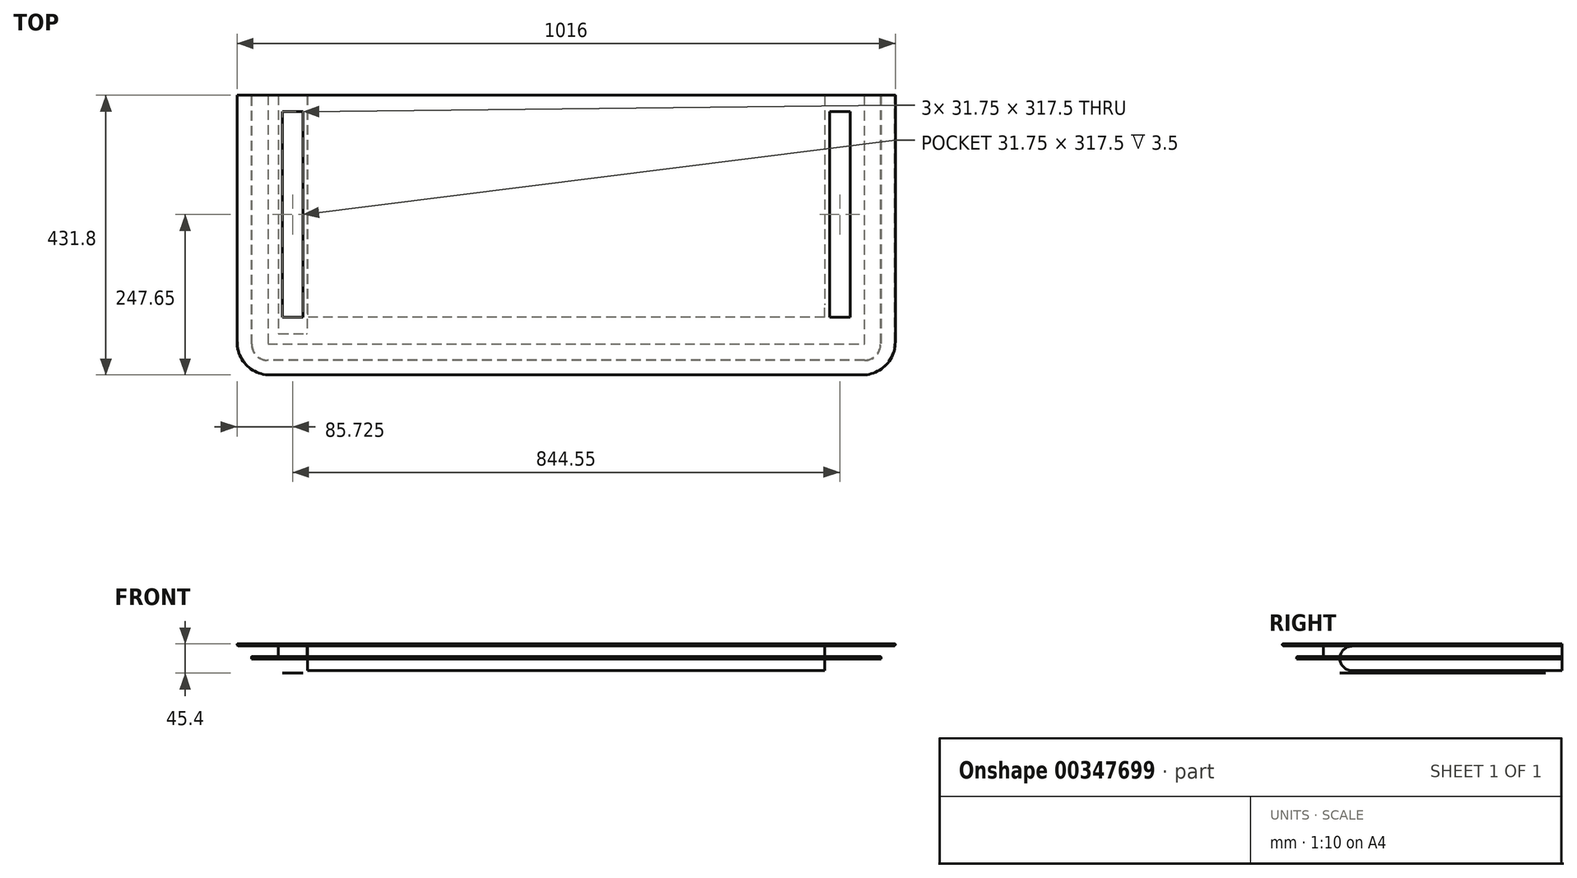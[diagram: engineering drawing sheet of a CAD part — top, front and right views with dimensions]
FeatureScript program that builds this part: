
annotation { "Feature Type Name" : "Feature", "Feature Type Description" : "" }
export const myFeature = defineFeature(function(context is Context, id is Id, definition is map)
    precondition{}
    {
        {
            assignVariable(context, id + "F0", {"name" : "TopThickness", "anyValue" : 2.5});
        }
        {
            assignVariable(context, id + "F1", {"name" : "LegWidth", "anyValue" : 1.75});
        }
        {
            assignVariable(context, id + "F2", {"name" : "CoveHeight", "anyValue" : 1});
        }
        {
            assignVariable(context, id + "F3", {"name" : "BottomThickness", "anyValue" : 1.5});
        }
        {
            assignVariable(context, id + "F4", {"name" : "BottomSkirtHeight", "anyValue" : 2});
        }
        {
            assignVariable(context, id + "F5", {"name" : "LegHeight", "anyValue" : 24 - getVariable(context, 'TopThickness') - 1.5 * getVariable(context, 'CoveHeight') - getVariable(context, 'BottomThickness') - getVariable(context, 'BottomSkirtHeight')});
        }
        {
            var Q0;
            Q0=qCreatedBy(makeId("Top.planeOp"),FACE);
            var sketch = newSketch(context, id + "F6", { "sketchPlane" : qUnion([Q0])});
            skLineSegment(sketch, "E0.bottom", {"start": v(0, 0) * mm, "end": v(1016, 0) * mm});
            skLineSegment(sketch, "E0.top", {"start": v(0, 431.8) * mm, "end": v(1016, 431.8) * mm});
            skLineSegment(sketch, "E0.left", {"start": v(0, 0) * mm, "end": v(0, 431.8) * mm});
            skLineSegment(sketch, "E0.right", {"start": v(1016, 0) * mm, "end": v(1016, 431.8) * mm});
            skSolve(sketch);
        }
        {
            var Q0;
            Q0 = qSketchRegion(id + "F6", true);
            extrude(context, id + "F7", {"entities" : qUnion([Q0]), "oppositeDirection" : true, "depth" : (getVariable(context, 'TopThickness')) * mm});
        }
        {
            var Q0;
            Q0=makeQuery(id+"F7.opExtrude","SWEPT_EDGE",EDGE,{"disambiguationData":[OSD([sQuery(id+"F6.wireOp",EDGE,"E0.bottom"),sQuery(id+"F6.wireOp",EDGE,"E0.left")])]});
            var Q1;
            Q1=makeQuery(id+"F7.opExtrude","SWEPT_EDGE",EDGE,{"disambiguationData":[OSD([sQuery(id+"F6.wireOp",EDGE,"E0.bottom"),sQuery(id+"F6.wireOp",EDGE,"E0.right")])]});
            fillet(context, id + "F8", {"entities" : qUnion([Q0, Q1]), "radius" : 50.8 * mm, "tangentPropagation" : true, "allowEdgeOverflow" : false});
        }
        {
            var Q0;
            Q0=makeQuery(id+"F7.opExtrude","CAP_EDGE",EDGE,{"disambiguationData":[OSD([sQuery(id+"F6.wireOp",EDGE,"E0.left")])],"isStart":true});
            var Q1;
            Q1=makeQuery(id+"F7.opExtrude","CAP_EDGE",EDGE,{"disambiguationData":[OSD([sQuery(id+"F6.wireOp",EDGE,"E0.left")])],"isStart":false});
            fillet(context, id + "F9", {"entities" : qUnion([Q0, Q1]), "radius" : (getVariable(context, 'TopThickness') / 2) * mm, "tangentPropagation" : true, "allowEdgeOverflow" : false});
        }
        {
            var Q0;
            Q0=makeQuery(id+"F7.opExtrude","CAP_FACE",FACE,{"disambiguationData":[OSD([sQuery(id+"F6.wireOp",EDGE,"E0.bottom"),sQuery(id+"F6.wireOp",EDGE,"E0.top"),sQuery(id+"F6.wireOp",EDGE,"E0.left"),sQuery(id+"F6.wireOp",EDGE,"E0.right")])],"isStart":false});
            extrude(context, id + "F10", {"entities" : qUnion([Q0]), "operationType" : NewBodyOperationType.ADD, "depth" : (getVariable(context, 'CoveHeight')) * mm});
        }
        {
            var Q0;
            Q0=makeQuery(id+"F10.opExtrude","CAP_FACE",FACE,{"disambiguationData":[OSD([sQuery(id+"F6.wireOp",EDGE,"E0.bottom"),sQuery(id+"F6.wireOp",EDGE,"E0.top"),sQuery(id+"F6.wireOp",EDGE,"E0.left"),sQuery(id+"F6.wireOp",EDGE,"E0.right")])],"isStart":false});
            var sketch = newSketch(context, id + "F11", { "sketchPlane" : qUnion([Q0])});
            skLineSegment(sketch, "E1.0", {"start": v(31.75, -50.8) * mm, "end": v(31.75, -431.8) * mm});
            skArc(sketch, "E1.1", {"start": v(50.8, -31.75) * mm, "mid": v(37.33, -37.33) * mm, "end": v(31.75, -50.8) * mm});
            skLineSegment(sketch, "E1.2", {"start": v(965.2, -31.75) * mm, "end": v(50.8, -31.75) * mm});
            skArc(sketch, "E1.3", {"start": v(984.25, -50.8) * mm, "mid": v(978.67, -37.33) * mm, "end": v(965.2, -31.75) * mm});
            skLineSegment(sketch, "E1.4", {"start": v(984.25, -431.8) * mm, "end": v(984.25, -50.8) * mm});
            skSolve(sketch);
        }
        {
            var Q0;
            {var subQ0=sQuery(id+"F6.wireOp",EDGE,"E0.top");Q0=makeQuery(id+"F10.boolean.opBoolean","MERGE",FACE,{"derivedFrom":[makeQuery(id+"F7.opExtrude","SWEPT_FACE",FACE,{"disambiguationData":[OSD([subQ0])]}),makeQuery(id+"F10.opExtrude","SWEPT_FACE",FACE,{"disambiguationData":[OSD([subQ0])]})]});}
            var sketch = newSketch(context, id + "F12", { "sketchPlane" : qUnion([Q0])});
            skCircle(sketch, "E2", {"center": v(-31.75, -88.9) * mm, "radius": 19.05 * mm});
            skSolve(sketch);
        }
        {
            var Q0;
            {var subQ0=sQuery(id+"F12.wireOp",EDGE,"E2");var subQ3=sQuery(id+"F6.wireOp",EDGE,"E0.top");var subQ7=makeQuery(id+"F10.opExtrude","CAP_EDGE",EDGE,{"disambiguationData":[OSD([subQ3])],"isStart":false});var subQ8=makeQuery(id+"F12.imprint","INTERSECT",VERTEX,{"derivedFrom":[subQ7,subQ0]});Q0=makeQuery(id+"F12.imprint","IMPRINT",FACE,{"disambiguationData":[TD([[makeQuery(id+"F12.imprint","IMPRINT",EDGE,{"disambiguationData":[TD([[subQ8,1.0]])],"derivedFrom":subQ0}),1.0]])]});}
            var Q1;
            Q1=sQuery(id+"F11.wireOp",EDGE,"E1.0");
            var Q2;
            Q2=sQuery(id+"F11.wireOp",EDGE,"E1.1");
            var Q3;
            Q3=sQuery(id+"F11.wireOp",EDGE,"E1.2");
            var Q4;
            Q4=sQuery(id+"F11.wireOp",EDGE,"E1.3");
            var Q5;
            Q5=sQuery(id+"F11.wireOp",EDGE,"E1.4");
            sweep(context, id + "F13", {"operationType" : NewBodyOperationType.REMOVE, "profiles" : qUnion([Q0]), "path" : qUnion([Q1, Q2, Q3, Q4, Q5])});
        }
        {
            var Q0;
            Q0=makeQuery(id+"F10.opExtrude","CAP_FACE",FACE,{"disambiguationData":[OSD([sQuery(id+"F6.wireOp",EDGE,"E0.bottom"),sQuery(id+"F6.wireOp",EDGE,"E0.top"),sQuery(id+"F6.wireOp",EDGE,"E0.left"),sQuery(id+"F6.wireOp",EDGE,"E0.right")])],"isStart":false});
            var sketch = newSketch(context, id + "F14", { "sketchPlane" : qUnion([Q0])});
            skLineSegment(sketch, "E3.bottom", {"start": v(63.5, -431.8) * mm, "end": v(107.95, -431.8) * mm});
            skLineSegment(sketch, "E3.top", {"start": v(63.5, -63.5) * mm, "end": v(107.95, -63.5) * mm});
            skLineSegment(sketch, "E3.left", {"start": v(63.5, -431.8) * mm, "end": v(63.5, -63.5) * mm});
            skLineSegment(sketch, "E3.right", {"start": v(107.95, -431.8) * mm, "end": v(107.95, -63.5) * mm});
            skSolve(sketch);
        }
        {
            var Q0;
            Q0 = qSketchRegion(id + "F14", true);
            extrude(context, id + "F15", {"entities" : qUnion([Q0]), "depth" : (getVariable(context, 'LegHeight')) * mm});
        }
        {
            var Q0;
            Q0=makeQuery(id+"F15.opExtrude","CAP_FACE",FACE,{"disambiguationData":[OSD([sQuery(id+"F14.wireOp",EDGE,"E3.bottom"),sQuery(id+"F14.wireOp",EDGE,"E3.top"),sQuery(id+"F14.wireOp",EDGE,"E3.left"),sQuery(id+"F14.wireOp",EDGE,"E3.right")])],"isStart":true});
            var sketch = newSketch(context, id + "F16", { "sketchPlane" : qUnion([Q0])});
            skLineSegment(sketch, "E4.bottom", {"start": v(69.85, 406.4) * mm, "end": v(101.6, 406.4) * mm});
            skLineSegment(sketch, "E4.top", {"start": v(69.85, 88.9) * mm, "end": v(101.6, 88.9) * mm});
            skLineSegment(sketch, "E4.left", {"start": v(69.85, 406.4) * mm, "end": v(69.85, 88.9) * mm});
            skLineSegment(sketch, "E4.right", {"start": v(101.6, 406.4) * mm, "end": v(101.6, 88.9) * mm});
            skSolve(sketch);
        }
        {
            var Q0;
            Q0 = qSketchRegion(id + "F16", true);
            extrude(context, id + "F17", {"entities" : qUnion([Q0]), "operationType" : NewBodyOperationType.ADD, "depth" : 25.4 * mm});
        }
        {
            var Q0;
            Q0=makeQuery(id+"F10.opExtrude","CAP_FACE",FACE,{"disambiguationData":[OSD([sQuery(id+"F6.wireOp",EDGE,"E0.bottom"),sQuery(id+"F6.wireOp",EDGE,"E0.top"),sQuery(id+"F6.wireOp",EDGE,"E0.left"),sQuery(id+"F6.wireOp",EDGE,"E0.right")])],"isStart":false});
            var sketch = newSketch(context, id + "F18", { "sketchPlane" : qUnion([Q0])});
            skLineSegment(sketch, "E5.0.0", {"start": v(69.85, -406.4) * mm, "end": v(69.85, -88.9) * mm});
            skLineSegment(sketch, "E5.0.1", {"start": v(69.85, -88.9) * mm, "end": v(101.6, -88.9) * mm});
            skLineSegment(sketch, "E5.0.2", {"start": v(101.6, -88.9) * mm, "end": v(101.6, -406.4) * mm});
            skLineSegment(sketch, "E5.0.3", {"start": v(101.6, -406.4) * mm, "end": v(69.85, -406.4) * mm});
            skLineSegment(sketch, "E6", {"start": v(508, -431.8) * mm, "end": v(508, 183.64) * mm, "construction": true});
            skLineSegment(sketch, "E7.MirrorCS", {"start": v(914.4, -406.4) * mm, "end": v(946.15, -406.4) * mm});
            skLineSegment(sketch, "E8.MirrorCS", {"start": v(946.15, -88.9) * mm, "end": v(914.4, -88.9) * mm});
            skLineSegment(sketch, "E9.MirrorCS", {"start": v(946.15, -406.4) * mm, "end": v(946.15, -88.9) * mm});
            skLineSegment(sketch, "E10.MirrorCS", {"start": v(914.4, -88.9) * mm, "end": v(914.4, -406.4) * mm});
            skSolve(sketch);
        }
        {
            var Q0;
            Q0 = qSketchRegion(id + "F18", true);
            extrude(context, id + "F19", {"entities" : qUnion([Q0]), "operationType" : NewBodyOperationType.REMOVE, "oppositeDirection" : true, "depth" : 25.4 * mm});
        }
        {
            var Q0;
            Q0=makeQuery(id+"F15.opExtrude","CAP_FACE",FACE,{"disambiguationData":[OSD([sQuery(id+"F14.wireOp",EDGE,"E3.bottom"),sQuery(id+"F14.wireOp",EDGE,"E3.top"),sQuery(id+"F14.wireOp",EDGE,"E3.left"),sQuery(id+"F14.wireOp",EDGE,"E3.right")])],"isStart":false});
            var sketch = newSketch(context, id + "F20", { "sketchPlane" : qUnion([Q0])});
            skLineSegment(sketch, "E11.0.0", {"start": v(69.85, -406.4) * mm, "end": v(69.85, -88.9) * mm});
            skLineSegment(sketch, "E11.0.1", {"start": v(69.85, -88.9) * mm, "end": v(101.6, -88.9) * mm});
            skLineSegment(sketch, "E11.0.2", {"start": v(101.6, -88.9) * mm, "end": v(101.6, -406.4) * mm});
            skLineSegment(sketch, "E11.0.3", {"start": v(101.6, -406.4) * mm, "end": v(69.85, -406.4) * mm});
            skSolve(sketch);
        }
        {
            var Q0;
            Q0 = qSketchRegion(id + "F20", true);
            extrude(context, id + "F21", {"entities" : qUnion([Q0]), "operationType" : NewBodyOperationType.ADD, "depth" : 25.4 * mm});
        }
        {
            var Q0;
            Q0=makeQuery(id+"F15.opExtrude","SWEPT_EDGE",EDGE,{"disambiguationData":[OSD([sQuery(id+"F14.wireOp",EDGE,"E3.top"),sQuery(id+"F14.wireOp",EDGE,"E3.left")])]});
            var Q1;
            Q1=makeQuery(id+"F15.opExtrude","SWEPT_EDGE",EDGE,{"disambiguationData":[OSD([sQuery(id+"F14.wireOp",EDGE,"E3.top"),sQuery(id+"F14.wireOp",EDGE,"E3.right")])]});
            fillet(context, id + "F22", {"entities" : qUnion([Q0, Q1]), "radius" : (getVariable(context, 'LegWidth') / 2) * mm, "tangentPropagation" : true, "allowEdgeOverflow" : false});
        }
        {
            var Q0;
            Q0=makeQuery(id+"F15.opExtrude","CAP_FACE",FACE,{"disambiguationData":[OSD([sQuery(id+"F14.wireOp",EDGE,"E3.bottom"),sQuery(id+"F14.wireOp",EDGE,"E3.top"),sQuery(id+"F14.wireOp",EDGE,"E3.left"),sQuery(id+"F14.wireOp",EDGE,"E3.right")])],"isStart":false});
            var sketch = newSketch(context, id + "F23", { "sketchPlane" : qUnion([Q0])});
            skLineSegment(sketch, "E12.0", {"start": v(22.22, -22.22) * mm, "end": v(22.22, -460.38) * mm});
            skLineSegment(sketch, "E12.1", {"start": v(993.78, -22.22) * mm, "end": v(22.22, -22.22) * mm});
            skLineSegment(sketch, "E12.2", {"start": v(993.77, -460.38) * mm, "end": v(993.78, -22.22) * mm});
            skLineSegment(sketch, "E12.3", {"start": v(22.22, -460.38) * mm, "end": v(993.77, -460.38) * mm, "construction": true});
            skLineSegment(sketch, "E13", {"start": v(22.23, -431.8) * mm, "end": v(993.77, -431.8) * mm});
            skSolve(sketch);
        }
        {
            var Q0;
            Q0 = qSketchRegion(id + "F23", true);
            extrude(context, id + "F24", {"entities" : qUnion([Q0]), "depth" : (getVariable(context, 'BottomThickness')) * mm});
        }
        {
            var Q0;
            Q0=makeQuery(id+"F24.opExtrude","SWEPT_EDGE",EDGE,{"disambiguationData":[OSD([sQuery(id+"F23.wireOp",EDGE,"E12.0"),sQuery(id+"F23.wireOp",EDGE,"E12.1")])]});
            var Q1;
            Q1=makeQuery(id+"F24.opExtrude","SWEPT_EDGE",EDGE,{"disambiguationData":[OSD([sQuery(id+"F23.wireOp",EDGE,"E12.1"),sQuery(id+"F23.wireOp",EDGE,"E12.2")])]});
            fillet(context, id + "F25", {"entities" : qUnion([Q0, Q1]), "radius" : 25.4 * mm, "tangentPropagation" : true, "allowEdgeOverflow" : false});
        }
        {
            var Q0;
            Q0=makeQuery(id+"F24.opExtrude","CAP_EDGE",EDGE,{"disambiguationData":[OSD([sQuery(id+"F23.wireOp",EDGE,"E12.0")])],"isStart":true});
            fillet(context, id + "F26", {"entities" : qUnion([Q0]), "radius" : (.5 * getVariable(context, 'BottomThickness')) * mm, "tangentPropagation" : true, "allowEdgeOverflow" : false});
        }
        {
            var Q0;
            Q0=makeQuery(id+"F24.opExtrude","CAP_FACE",FACE,{"disambiguationData":[OSD([sQuery(id+"F23.wireOp",EDGE,"E12.0"),sQuery(id+"F23.wireOp",EDGE,"E12.1"),sQuery(id+"F23.wireOp",EDGE,"E12.2"),sQuery(id+"F23.wireOp",EDGE,"E13")])],"isStart":true});
            extrude(context, id + "F27", {"entities" : qUnion([Q0]), "operationType" : NewBodyOperationType.ADD, "depth" : (getVariable(context, 'CoveHeight') / 2) * mm});
        }
        {
            var Q0;
            Q0=makeQuery(id+"F27.opExtrude","CAP_FACE",FACE,{"disambiguationData":[OSD([sQuery(id+"F23.wireOp",EDGE,"E12.0"),sQuery(id+"F23.wireOp",EDGE,"E12.1"),sQuery(id+"F23.wireOp",EDGE,"E12.2"),sQuery(id+"F23.wireOp",EDGE,"E13")])],"isStart":false});
            var sketch = newSketch(context, id + "F28", { "sketchPlane" : qUnion([Q0])});
            skLineSegment(sketch, "E14.0", {"start": v(41.28, 431.8) * mm, "end": v(41.28, 47.63) * mm});
            skArc(sketch, "E14.1", {"start": v(41.27, 47.63) * mm, "mid": v(43.13, 43.13) * mm, "end": v(47.62, 41.28) * mm});
            skLineSegment(sketch, "E15.0", {"start": v(47.62, 41.27) * mm, "end": v(968.38, 41.27) * mm});
            skArc(sketch, "E16.0", {"start": v(968.38, 41.27) * mm, "mid": v(972.87, 43.13) * mm, "end": v(974.72, 47.62) * mm});
            skLineSegment(sketch, "E17.0", {"start": v(974.73, 47.62) * mm, "end": v(974.73, 431.8) * mm});
            skSolve(sketch);
        }
        {
            var Q0;
            {var subQ0=sQuery(id+"F23.wireOp",EDGE,"E13");Q0=makeQuery(id+"F27.boolean.opBoolean","MERGE",FACE,{"derivedFrom":[makeQuery(id+"F24.opExtrude","SWEPT_FACE",FACE,{"disambiguationData":[OSD([subQ0])]}),makeQuery(id+"F27.opExtrude","SWEPT_FACE",FACE,{"disambiguationData":[OSD([subQ0])]})]});}
            var sketch = newSketch(context, id + "F29", { "sketchPlane" : qUnion([Q0])});
            skCircle(sketch, "E18", {"center": v(-974.72, -495.3) * mm, "radius": 6.35 * mm});
            skSolve(sketch);
        }
        {
            var Q0;
            Q0 = qSketchRegion(id + "F29", true);
            var Q1;
            Q1 = qConstructionFilter(qBodyType(qCreatedBy(id + "F28" ,EDGE), BodyType.WIRE), ConstructionObject.NO);
            sweep(context, id + "F30", {"operationType" : NewBodyOperationType.REMOVE, "profiles" : qUnion([Q0]), "path" : qUnion([Q1])});
        }
        {
            var Q0;
            Q0=makeQuery(id+"F27.opExtrude","CAP_FACE",FACE,{"disambiguationData":[OSD([sQuery(id+"F23.wireOp",EDGE,"E12.0"),sQuery(id+"F23.wireOp",EDGE,"E12.1"),sQuery(id+"F23.wireOp",EDGE,"E12.2"),sQuery(id+"F23.wireOp",EDGE,"E13")])],"isStart":false});
            var sketch = newSketch(context, id + "F31", { "sketchPlane" : qUnion([Q0])});
            skLineSegment(sketch, "E19.0.0", {"start": v(69.85, 406.4) * mm, "end": v(101.6, 406.4) * mm});
            skLineSegment(sketch, "E19.0.1", {"start": v(101.6, 406.4) * mm, "end": v(101.6, 88.9) * mm});
            skLineSegment(sketch, "E19.0.2", {"start": v(101.6, 88.9) * mm, "end": v(69.85, 88.9) * mm});
            skLineSegment(sketch, "E19.0.3", {"start": v(69.85, 88.9) * mm, "end": v(69.85, 406.4) * mm});
            skLineSegment(sketch, "E20", {"start": v(508, 431.8) * mm, "end": v(508, -9.25) * mm, "construction": true});
            skLineSegment(sketch, "E21.MirrorCS", {"start": v(914.4, 88.9) * mm, "end": v(946.15, 88.9) * mm});
            skLineSegment(sketch, "E22.MirrorCS", {"start": v(914.4, 406.4) * mm, "end": v(914.4, 88.9) * mm});
            skLineSegment(sketch, "E23.MirrorCS", {"start": v(946.15, 406.4) * mm, "end": v(914.4, 406.4) * mm});
            skLineSegment(sketch, "E24.MirrorCS", {"start": v(946.15, 88.9) * mm, "end": v(946.15, 406.4) * mm});
            skSolve(sketch);
        }
        {
            var Q0;
            Q0 = qSketchRegion(id + "F31", true);
            extrude(context, id + "F32", {"entities" : qUnion([Q0]), "operationType" : NewBodyOperationType.REMOVE, "oppositeDirection" : true, "depth" : 25.4 * mm});
        }
        {
            var Q0;
            Q0=makeQuery(id+"F10.opExtrude","CAP_FACE",FACE,{"disambiguationData":[OSD([sQuery(id+"F6.wireOp",EDGE,"E0.bottom"),sQuery(id+"F6.wireOp",EDGE,"E0.top"),sQuery(id+"F6.wireOp",EDGE,"E0.left"),sQuery(id+"F6.wireOp",EDGE,"E0.right")])],"isStart":false});
            var sketch = newSketch(context, id + "F33", { "sketchPlane" : qUnion([Q0])});
            skLineSegment(sketch, "E25", {"start": v(508, -431.8) * mm, "end": v(508, -88.9) * mm, "construction": true});
            skLineSegment(sketch, "E26", {"start": v(508, -431.8) * mm, "end": v(508, -431.8) * mm});
            skLineSegment(sketch, "E27", {"start": v(508, -431.8) * mm, "end": v(109.1, -431.8) * mm});
            skLineSegment(sketch, "E28", {"start": v(109.1, -431.8) * mm, "end": v(109.1, -88.9) * mm});
            skLineSegment(sketch, "E29", {"start": v(109.1, -88.9) * mm, "end": v(508, -88.9) * mm});
            skLineSegment(sketch, "E30.MirrorCS", {"start": v(906.9, -88.9) * mm, "end": v(508, -88.9) * mm});
            skLineSegment(sketch, "E31.MirrorCS", {"start": v(906.9, -431.8) * mm, "end": v(906.9, -88.9) * mm});
            skLineSegment(sketch, "E32.MirrorCS", {"start": v(508, -431.8) * mm, "end": v(906.9, -431.8) * mm});
            skSolve(sketch);
        }
        {
            var Q0;
            Q0 = qSketchRegion(id + "F33", true);
            extrude(context, id + "F34", {"entities" : qUnion([Q0]), "depth" : 38.1 * mm});
        }
        {
            var Q0;
            Q0=makeQuery(id+"F34.opExtrude","CAP_EDGE",EDGE,{"disambiguationData":[OSD([sQuery(id+"F33.wireOp",EDGE,"E29"),sQuery(id+"F33.wireOp",EDGE,"E30.MirrorCS")])],"isStart":true});
            var Q1;
            Q1=makeQuery(id+"F34.opExtrude","CAP_EDGE",EDGE,{"disambiguationData":[OSD([sQuery(id+"F33.wireOp",EDGE,"E29"),sQuery(id+"F33.wireOp",EDGE,"E30.MirrorCS")])],"isStart":false});
            fillet(context, id + "F35", {"entities" : qUnion([Q0, Q1]), "radius" : 19.3 * mm, "tangentPropagation" : true, "allowEdgeOverflow" : false});
        }
        {
            var Q0;
            Q0=makeQuery(id+"F24.opExtrude","CAP_FACE",FACE,{"disambiguationData":[OSD([sQuery(id+"F23.wireOp",EDGE,"E12.0"),sQuery(id+"F23.wireOp",EDGE,"E12.1"),sQuery(id+"F23.wireOp",EDGE,"E12.2"),sQuery(id+"F23.wireOp",EDGE,"E13")])],"isStart":false});
            var sketch = newSketch(context, id + "F36", { "sketchPlane" : qUnion([Q0])});
            skLineSegment(sketch, "E33.0", {"start": v(22.22, -47.63) * mm, "end": v(22.22, -431.8) * mm});
            skArc(sketch, "E34.0", {"start": v(47.62, -22.23) * mm, "mid": v(29.66, -29.66) * mm, "end": v(22.22, -47.63) * mm});
            skLineSegment(sketch, "E35.0", {"start": v(968.38, -22.22) * mm, "end": v(47.62, -22.22) * mm});
            skArc(sketch, "E36.0", {"start": v(993.77, -47.62) * mm, "mid": v(986.34, -29.66) * mm, "end": v(968.38, -22.22) * mm});
            skLineSegment(sketch, "E37.0", {"start": v(993.77, -431.8) * mm, "end": v(993.78, -47.62) * mm});
            skLineSegment(sketch, "E38", {"start": v(22.22, -431.8) * mm, "end": v(47.62, -431.8) * mm});
            skLineSegment(sketch, "E39", {"start": v(47.62, -431.8) * mm, "end": v(47.62, -47.63) * mm});
            skLineSegment(sketch, "E40", {"start": v(47.63, -47.63) * mm, "end": v(968.38, -47.62) * mm});
            skLineSegment(sketch, "E41", {"start": v(968.38, -47.62) * mm, "end": v(968.38, -431.8) * mm});
            skLineSegment(sketch, "E42", {"start": v(968.38, -431.8) * mm, "end": v(993.77, -431.8) * mm});
            skSolve(sketch);
        }
        {
            var Q0;
            Q0 = qSketchRegion(id + "F36", true);
            extrude(context, id + "F37", {"entities" : qUnion([Q0]), "operationType" : NewBodyOperationType.ADD, "depth" : (getVariable(context, 'BottomSkirtHeight')) * mm});
        }
    });
